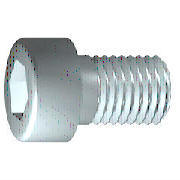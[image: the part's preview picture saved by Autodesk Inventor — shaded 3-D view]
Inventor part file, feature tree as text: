
AUTODESK INVENTOR PART (.ipt)
format: ipt  version: 2018 (Build 220112000, 112)  size: 192,512 bytes
history: native  units: mm (DEFAULTED — no unit token found)
features: sketch x2, extrude x1, plane x1, fillet x1
ambient origin geometry x7: Origin, YZ Plane, XY Plane, X Axis, Y Axis, Z Axis, Center Point
bodies: Solid1 (feature_tree), Body (feature_tree)
feature tree (5):
  extrude  "Slot"  Depth=5.0mm
  plane  "Work Plane1"
  fillet  "Fillet2"  Radius=5.0mm
  sketch  "Sketch1"  dims[d1=9.90924mm d2=0.49086mm d3=5.0mm]
  sketch  "Sketch2"  dims[d4=2.5mm d5=60.0deg d6=5.0mm d7=5.0mm d8=4.618802mm d9=8.5mm d10=90.0deg d11=10.0mm d12=0.0mm d13=9.90924mm d14=0.0mm d15=0.49076mm d16=0.49076mm d17=0.5mm d19=0.0mm d26=12.0mm d27=45.0deg d28=0.0mm d29=0.0mm d30=0.1mm]
